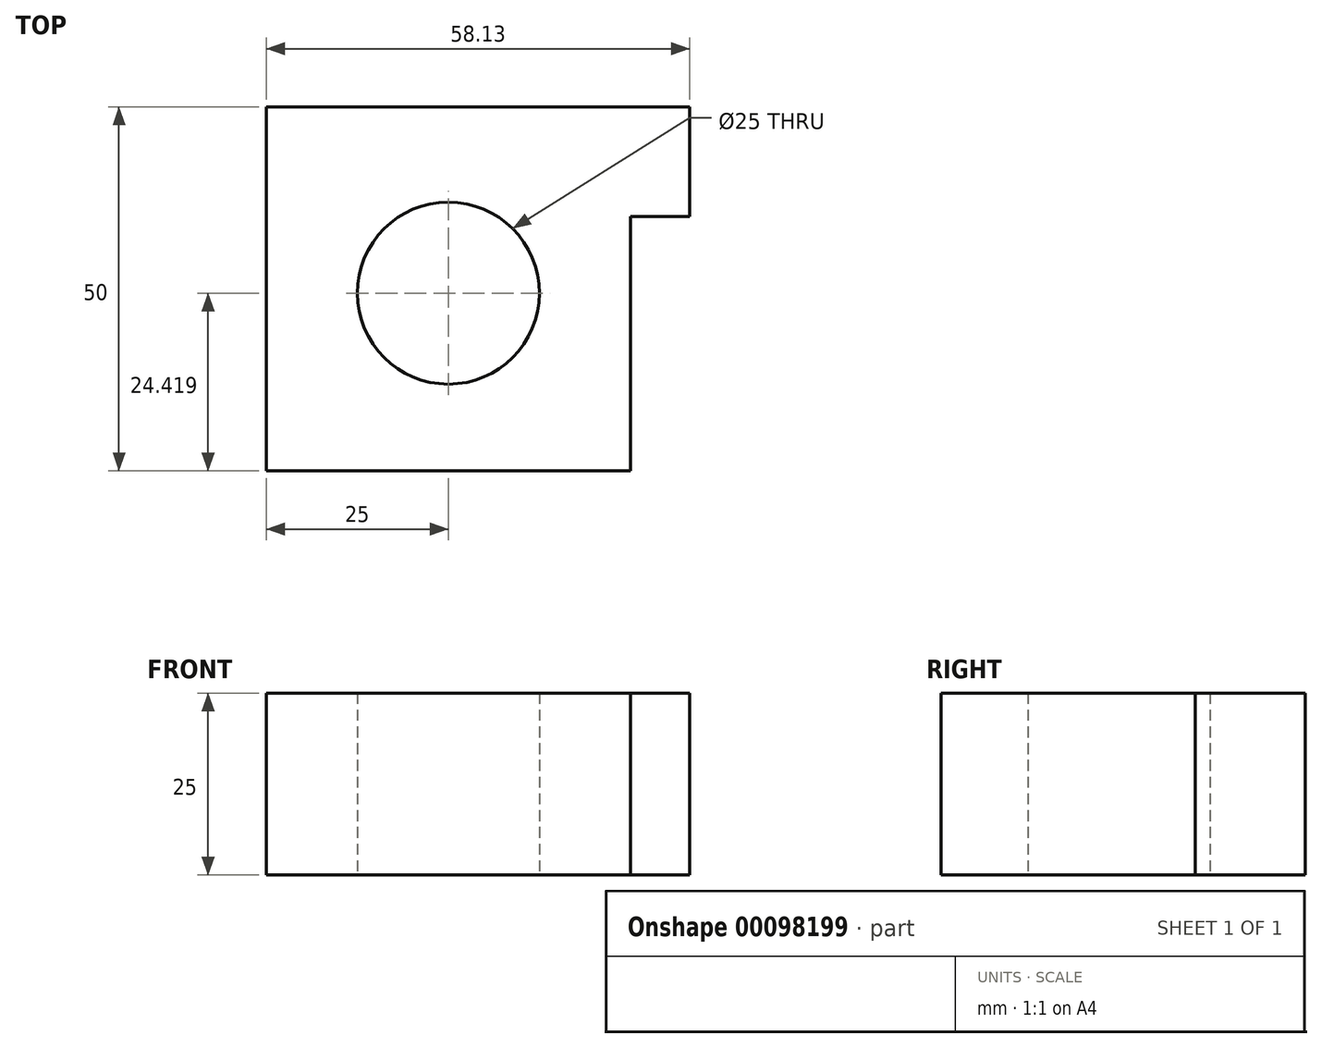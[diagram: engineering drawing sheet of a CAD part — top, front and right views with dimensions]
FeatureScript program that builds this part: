
annotation { "Feature Type Name" : "Feature", "Feature Type Description" : "" }
export const myFeature = defineFeature(function(context is Context, id is Id, definition is map)
    precondition{}
    {
        {
            var Q0;
            Q0=qCreatedBy(makeId("Top.planeOp"),FACE);
            var sketch = newSketch(context, id + "F0", { "sketchPlane" : qUnion([Q0])});
            skLineSegment(sketch, "E0.bottom", {"start": v(0, 0) * mm, "end": v(-50, 0) * mm});
            skLineSegment(sketch, "E0.top", {"start": v(0, 50) * mm, "end": v(-50, 50) * mm});
            skLineSegment(sketch, "E0.left", {"start": v(0, 0) * mm, "end": v(0, 50) * mm});
            skLineSegment(sketch, "E0.right", {"start": v(-50, 0) * mm, "end": v(-50, 50) * mm});
            skCircle(sketch, "E1", {"center": v(-25, 24.42) * mm, "radius": 12.5 * mm});
            skPoint(sketch, "E1.centerSnap0", {"position": v(-25, 50) * mm});
            skLineSegment(sketch, "E2.bottom", {"start": v(0, 50) * mm, "end": v(8.13, 50) * mm});
            skLineSegment(sketch, "E2.top", {"start": v(0, 34.93) * mm, "end": v(8.13, 34.93) * mm});
            skLineSegment(sketch, "E2.left", {"start": v(0, 50) * mm, "end": v(0, 34.93) * mm});
            skLineSegment(sketch, "E2.right", {"start": v(8.13, 50) * mm, "end": v(8.13, 34.93) * mm});
            skSolve(sketch);
        }
        {
            var Q0;
            Q0=makeQuery(id+"F0.imprint","IMPRINT",FACE,{"disambiguationData":[TD([[makeQuery(id+"F0.imprint","IMPRINT",EDGE,{"derivedFrom":sQuery(id+"F0.wireOp",EDGE,"E0.bottom")}),-1.0]])]});
            var Q1;
            Q1=makeQuery(id+"F0.imprint","IMPRINT",FACE,{"disambiguationData":[TD([[makeQuery(id+"F0.imprint","IMPRINT",EDGE,{"derivedFrom":sQuery(id+"F0.wireOp",EDGE,"E2.bottom")}),-1.0]])]});
            extrude(context, id + "F1", {"entities" : qUnion([Q0, Q1]), "depth" : 25 * mm});
        }
    });
